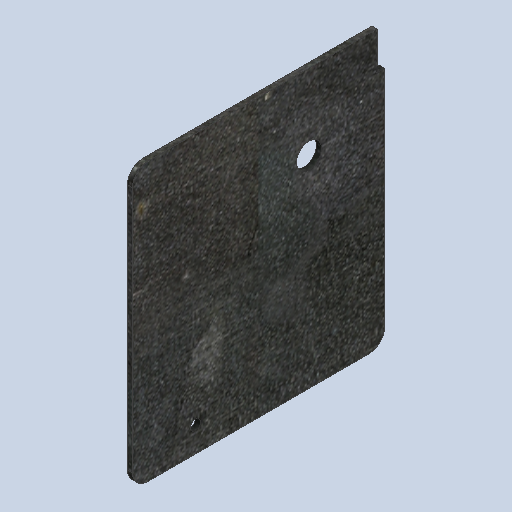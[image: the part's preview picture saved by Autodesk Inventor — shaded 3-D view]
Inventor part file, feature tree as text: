
AUTODESK INVENTOR PART (.ipt)
format: ipt  version: 2024.3 (Build 283343000, 343)  size: 279,040 bytes
history: native  units: mm
features: sheet_metal_op x1, chamfer x1, sketch x1, other x1
ambient origin geometry x8: Origin, YZ Plane, XZ Plane, XY Plane, X Axis, Y Axis, Z Axis, Center Point
bodies: Body1 (feature_tree)
feature tree (4):
  sheet_metal_op  "Face2"
  chamfer  "Corner Round2"
  sketch  "Sketch1"  dims[d0=110.0mm d1=100.0mm d2=3.0mm d3=15.0mm d4=4.0mm d5=10.0mm d6=25.0mm d9=10.0mm d10=30.0mm d11=30.0mm d12=2.0mm d13=6.0mm]
  other  "Plate2"
